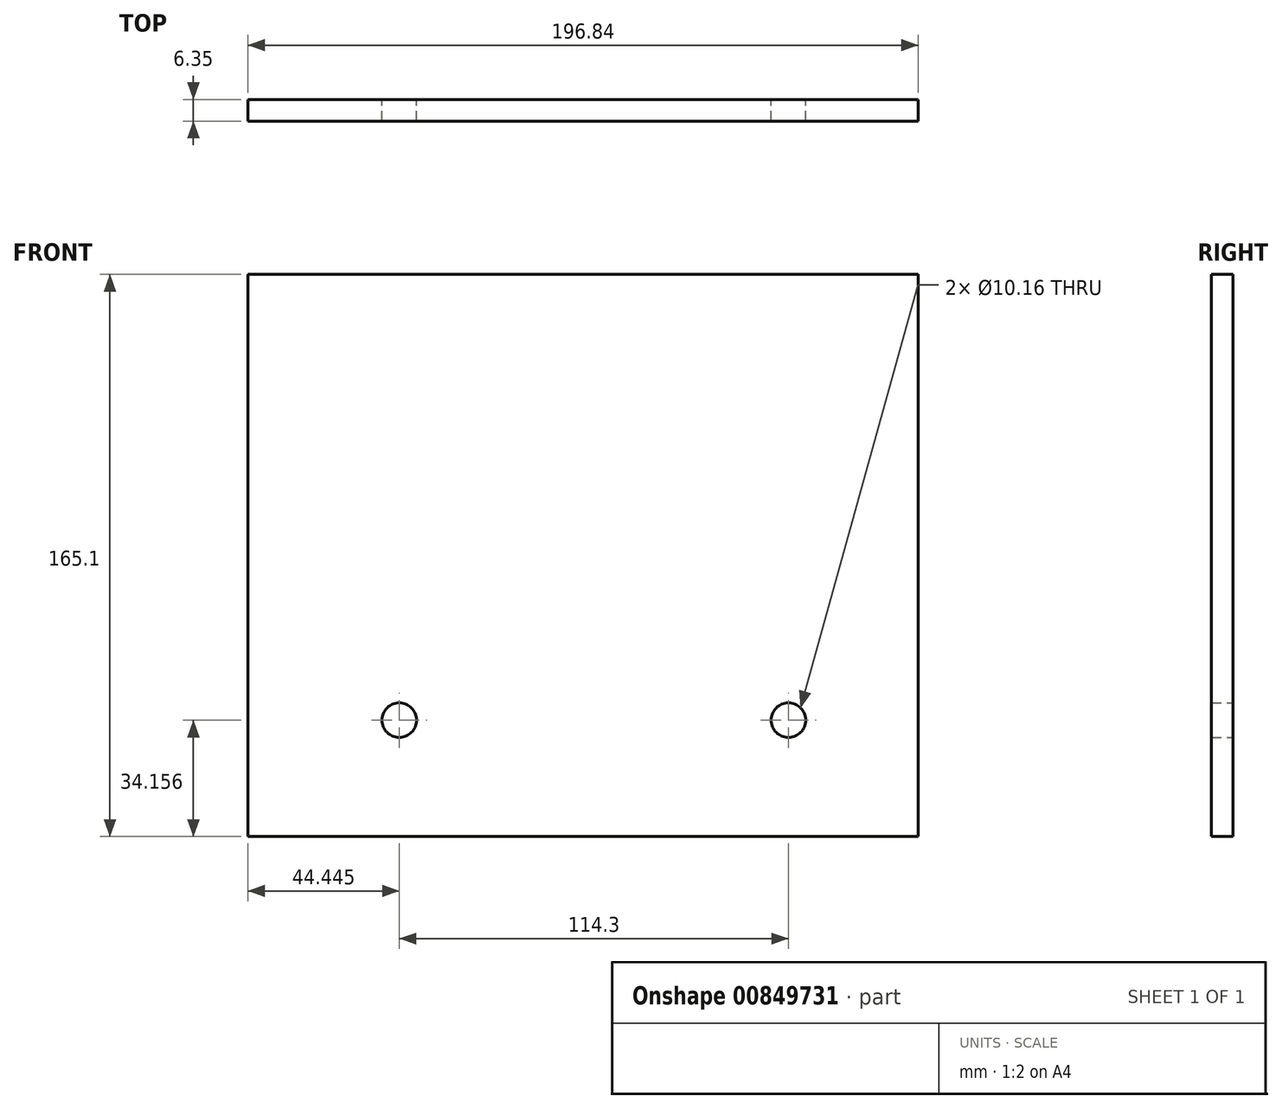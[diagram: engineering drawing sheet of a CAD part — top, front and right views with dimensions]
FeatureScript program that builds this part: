
annotation { "Feature Type Name" : "Feature", "Feature Type Description" : "" }
export const myFeature = defineFeature(function(context is Context, id is Id, definition is map)
    precondition{}
    {
        {
            var Q0;
            Q0=qCreatedBy(makeId("Front.planeOp"),FACE);
            var sketch = newSketch(context, id + "F0", { "sketchPlane" : qUnion([Q0])});
            skLineSegment(sketch, "E0.bottom", {"start": v(98.43, -82.55) * mm, "end": v(-98.42, -82.55) * mm});
            skLineSegment(sketch, "E0.top", {"start": v(98.42, 82.55) * mm, "end": v(-98.43, 82.55) * mm});
            skLineSegment(sketch, "E0.left", {"start": v(98.43, -82.55) * mm, "end": v(98.42, 82.55) * mm});
            skLineSegment(sketch, "E0.right", {"start": v(-98.42, -82.55) * mm, "end": v(-98.43, 82.55) * mm});
            skPoint(sketch, "E0.middle", {"position": v(0, 0) * mm});
            skCircle(sketch, "E1", {"center": v(60.33, -48.4) * mm, "radius": 5.08 * mm});
            skCircle(sketch, "E2", {"center": v(-53.97, -48.4) * mm, "radius": 5.08 * mm});
            skSolve(sketch);
        }
        {
            var Q0;
            Q0 = qSketchRegion(id + "F0", true);
            extrude(context, id + "F1", {"entities" : qUnion([Q0]), "depth" : 6.35 * mm, "offsetDistance" : 25.4 * mm});
        }
    });
